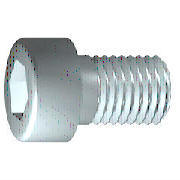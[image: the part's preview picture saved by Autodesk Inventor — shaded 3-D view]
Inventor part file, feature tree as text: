
AUTODESK INVENTOR PART (.ipt)
format: ipt  version: 2016 (Build 200138000, 138)  size: 189,952 bytes
history: native  units: mm (DEFAULTED — no unit token found)
features: sketch x2, extrude x1, plane x1, fillet x1
ambient origin geometry x7: Origin, YZ Plane, XY Plane, X Axis, Y Axis, Z Axis, Center Point
bodies: Solid1 (feature_tree), Body (feature_tree)
feature tree (5):
  extrude  "Slot"  Depth=4.0mm
  plane  "Work Plane1"
  fillet  "Fillet2"  Radius=4.0mm
  sketch  "Sketch1"  dims[d1=20.0mm d2=0.429515mm d3=4.0mm]
  sketch  "Sketch2"  dims[d4=2.0mm d5=60.0deg d6=4.0mm d7=4.0mm d8=3.464102mm d9=7.0mm d10=90.0deg d11=10.0mm d12=0.0mm d13=20.0mm d14=0.0mm d15=0.429415mm d16=0.429415mm d17=0.4mm d19=0.0mm d26=30.0mm d27=45.0deg d28=0.0mm d29=0.0mm d30=0.1mm]
